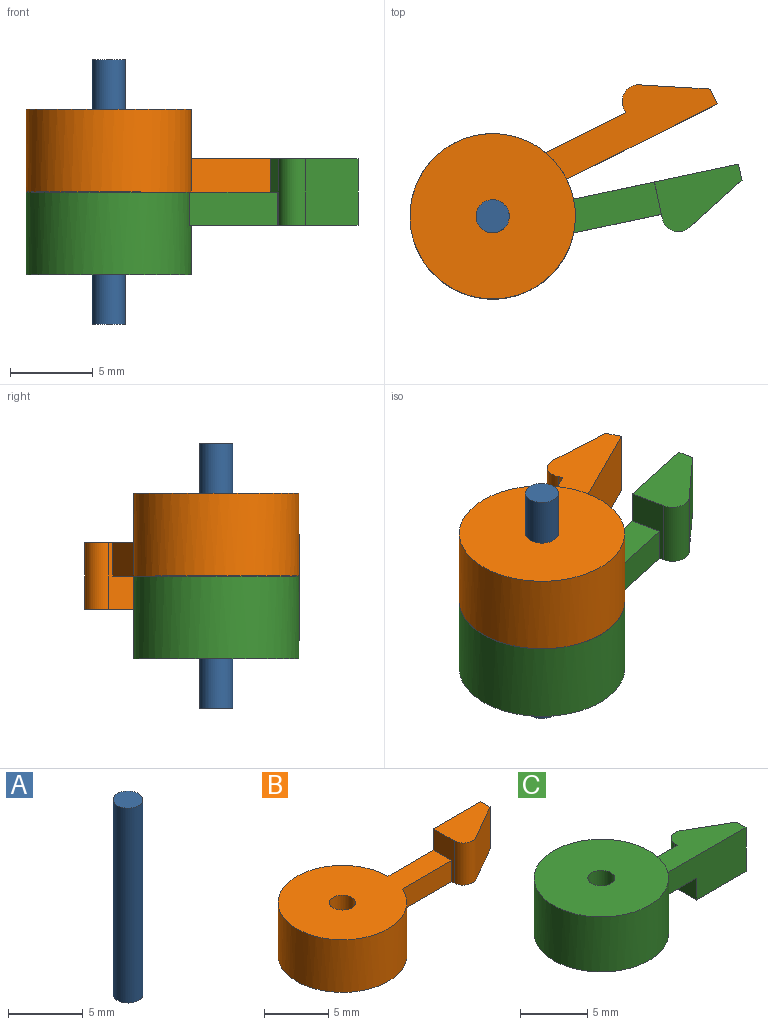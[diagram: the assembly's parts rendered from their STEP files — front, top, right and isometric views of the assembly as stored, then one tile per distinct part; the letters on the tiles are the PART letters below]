
ASSEMBLY  parts=3 mates=2
PART A: 3 faces, bbox 2x2x16 mm
  f0: cylinder r=1mm len=16mm, axis (0,0,-1), area 100.5mm2, adj f1,f2
  f1: plane 2x2mm, normal (0,0,1), area 3.1mm2, adj f0
  f2: plane 2x2mm, normal (0,0,-1), area 3.1mm2, adj f0
PART B: 12 faces, bbox 20.2x10x7 mm
  f0: cylinder r=5mm len=10mm, axis (0,0,1), area 153mm2, adj f1,f2,f3,f4,f5
  f1: plane 10x10mm, normal (0,0,-1), area 75.4mm2, adj f0,f11
  f2: plane 15x10mm, normal (0,0,1), area 85.7mm2, adj f0,f3,f4,f6,f11
  f3: plane 10.2x4mm, normal (0,1,0), area 30.8mm2, adj f0,f2,f5,f6,f8,f9
  f4: plane 5.42x2mm, normal (0,-1,0), area 10.8mm2, adj f0,f2,f5,f6
  f5: plane 10.61x3.27mm, normal (0,0,-1), area 22.6mm2, adj f0,f3,f4,f6,f7,f8,f10
  f6: plane 4x2.27mm, normal (-1,0,0), area 5.1mm2, adj f2,f3,f4,f5,f9,f10
  f7: plane 4x3.7mm, normal (0.5,-0.87,0), area 17.1mm2, adj f5,f8,f9,f10
  f8: plane 4x1mm, normal (1,0,0), area 4mm2, adj f3,f5,f7,f9
  f9: plane 5.2x3.27mm, normal (0,0,1), area 12.3mm2, adj f3,f6,f7,f8,f10
  f10: cylinder r=1mm len=4mm, axis (0,0,-1), area 8.4mm2, adj f5,f6,f7,f9
  f11: cylinder r=1mm len=5mm, axis (0,0,1), area 31.4mm2, adj f1,f2
PART C: 12 faces, bbox 20.2x10x7 mm
  f0: cylinder r=5mm len=10mm, axis (0,0,-1), area 153mm2, adj f1,f2,f3,f4,f5
  f1: plane 10x10mm, normal (0,0,1), area 75.4mm2, adj f0,f11
  f2: plane 15x10mm, normal (0,0,-1), area 85.7mm2, adj f0,f3,f4,f8,f11
  f3: plane 10.2x4mm, normal (0,-1,0), area 30.8mm2, adj f0,f2,f5,f6,f8,f9
  f4: plane 5.42x2mm, normal (0,1,0), area 10.8mm2, adj f0,f2,f5,f8
  f5: plane 10.61x3.27mm, normal (0,0,1), area 22.6mm2, adj f0,f3,f4,f6,f7,f8,f10
  f6: plane 4x1mm, normal (1,0,0), area 4mm2, adj f3,f5,f7,f9
  f7: plane 4x3.7mm, normal (0.5,0.87,0), area 17.1mm2, adj f5,f6,f9,f10
  f8: plane 4x2.27mm, normal (-1,0,0), area 5.1mm2, adj f2,f3,f4,f5,f9,f10
  f9: plane 5.2x3.27mm, normal (0,0,-1), area 12.3mm2, adj f3,f6,f7,f8,f10
  f10: cylinder r=1mm len=4mm, axis (0,0,-1), area 8.4mm2, adj f5,f7,f8,f9
  f11: cylinder r=1mm len=5mm, axis (0,0,-1), area 31.4mm2, adj f1,f2
PLACE A at identity fixed
PLACE B rot(axis=(0.97,0.23,0),180deg) t=(0,0,8)mm
PLACE C rot(axis=(0.99,0.1,0),180deg) t=(0,0,8)mm
MATE revolute A.f0 <-> B.f0  axis (0,0,-1) through (0,0,8)mm
MATE revolute C.f0 <-> A.f0  axis (0,0,1) through (0,0,8)mm
